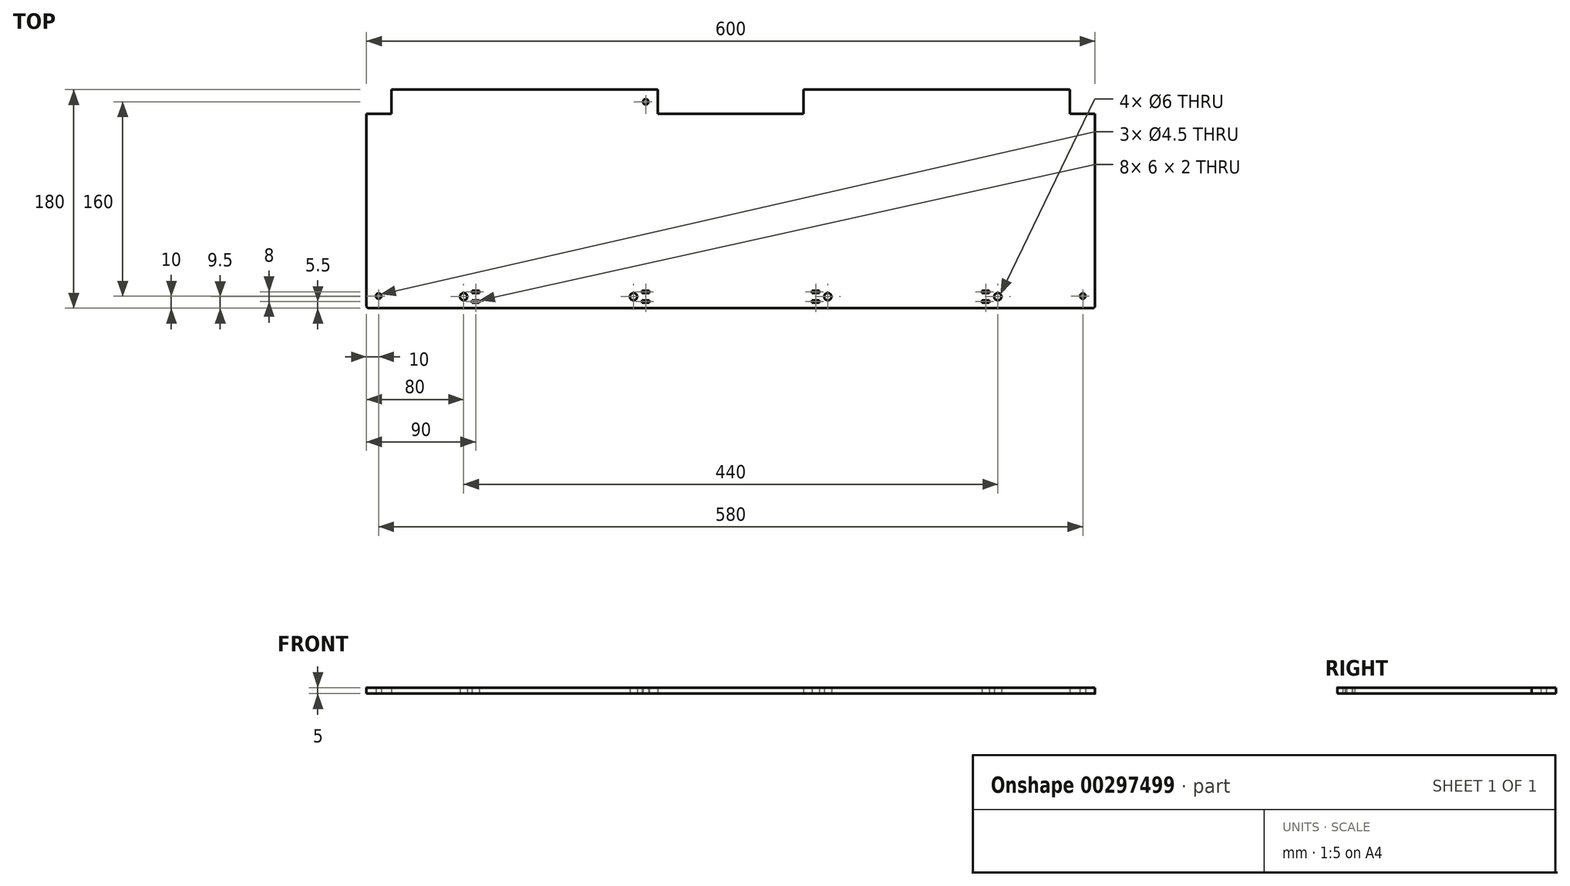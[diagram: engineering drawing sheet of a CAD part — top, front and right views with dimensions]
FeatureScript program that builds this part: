
annotation { "Feature Type Name" : "Feature", "Feature Type Description" : "" }
export const myFeature = defineFeature(function(context is Context, id is Id, definition is map)
    precondition{}
    {
        {
            var Q0;
            Q0=qCreatedBy(makeId("Top.planeOp"),FACE);
            var sketch = newSketch(context, id + "F0", { "sketchPlane" : qUnion([Q0])});
            skCircle(sketch, "E0", {"center": v(-70, 0) * mm, "radius": 3 * mm});
            skCircle(sketch, "E1.MirrorC", {"center": v(70, 0) * mm, "radius": 3 * mm});
            skCircle(sketch, "E2", {"center": v(230, 0) * mm, "radius": 3 * mm});
            skCircle(sketch, "E3.MirrorC", {"center": v(370, 0) * mm, "radius": 3 * mm});
            skLineSegment(sketch, "E4.bottom", {"start": v(-148, -9.5) * mm, "end": v(448, -9.5) * mm});
            skLineSegment(sketch, "E4.left", {"start": v(-150, -7.5) * mm, "end": v(-150, 150.5) * mm});
            skLineSegment(sketch, "E4.right", {"start": v(450, -7.5) * mm, "end": v(450, 150.5) * mm});
            skPoint(sketch, "E5.visualSharp", {"position": v(-150, -9.5) * mm});
            skArc(sketch, "E5.filletArc", {"start": v(-150, -7.5) * mm, "mid": v(-149.41, -8.91) * mm, "end": v(-148, -9.5) * mm});
            skPoint(sketch, "E6.visualSharp", {"position": v(450, -9.5) * mm});
            skArc(sketch, "E6.filletArc", {"start": v(448, -9.5) * mm, "mid": v(449.41, -8.91) * mm, "end": v(450, -7.5) * mm});
            skLineSegment(sketch, "E7", {"start": v(-129.5, 170.5) * mm, "end": v(90, 170.5) * mm});
            skLineSegment(sketch, "E8.top", {"start": v(-150, 150.5) * mm, "end": v(-129.5, 150.5) * mm});
            skLineSegment(sketch, "E8.right", {"start": v(-129.5, 170.5) * mm, "end": v(-129.5, 150.5) * mm});
            skLineSegment(sketch, "E9.top", {"start": v(450, 150.5) * mm, "end": v(429.5, 150.5) * mm});
            skLineSegment(sketch, "E9.right", {"start": v(429.5, 170.5) * mm, "end": v(429.5, 150.5) * mm});
            skLineSegment(sketch, "E10.top", {"start": v(210, 150.5) * mm, "end": v(90, 150.5) * mm});
            skLineSegment(sketch, "E10.left", {"start": v(210, 170.5) * mm, "end": v(210, 150.5) * mm});
            skLineSegment(sketch, "E10.right", {"start": v(90, 170.5) * mm, "end": v(90, 150.5) * mm});
            skPoint(sketch, "E10.middle", {"position": v(150, 160.5) * mm});
            skPoint(sketch, "E10.middle.positionSnap0", {"position": v(150, 170.5) * mm});
            skPoint(sketch, "E10.centerSnap0", {"position": v(150, 170.5) * mm});
            skPoint(sketch, "E11.orphan", {"position": v(-150, 170.5) * mm});
            skLineSegment(sketch, "E12.trimOffspring", {"start": v(210, 170.5) * mm, "end": v(429.5, 170.5) * mm});
            skPoint(sketch, "E13.orphan", {"position": v(450, 170.5) * mm});
            skCircle(sketch, "E14", {"center": v(-140, 0.5) * mm, "radius": 2.25 * mm});
            skCircle(sketch, "E15", {"center": v(440, 0.5) * mm, "radius": 2.25 * mm});
            skCircle(sketch, "E16", {"center": v(80, 160.5) * mm, "radius": 2.25 * mm});
            skLineSegment(sketch, "E17.bottom", {"start": v(-63, 5) * mm, "end": v(-57, 5) * mm});
            skLineSegment(sketch, "E17.top", {"start": v(-63, 3) * mm, "end": v(-57, 3) * mm});
            skLineSegment(sketch, "E17.left", {"start": v(-63, 5) * mm, "end": v(-63, 3) * mm});
            skLineSegment(sketch, "E17.right", {"start": v(-57, 5) * mm, "end": v(-57, 3) * mm});
            skLineSegment(sketch, "E18.bottom", {"start": v(-63, -3) * mm, "end": v(-57, -3) * mm});
            skLineSegment(sketch, "E18.top", {"start": v(-63, -5) * mm, "end": v(-57, -5) * mm});
            skLineSegment(sketch, "E18.left", {"start": v(-63, -3) * mm, "end": v(-63, -5) * mm});
            skLineSegment(sketch, "E18.right", {"start": v(-57, -3) * mm, "end": v(-57, -5) * mm});
            skLineSegment(sketch, "E19.bottom", {"start": v(77, 5) * mm, "end": v(83, 5) * mm});
            skLineSegment(sketch, "E19.top", {"start": v(77, 3) * mm, "end": v(83, 3) * mm});
            skLineSegment(sketch, "E19.left", {"start": v(77, 5) * mm, "end": v(77, 3) * mm});
            skLineSegment(sketch, "E19.right", {"start": v(83, 5) * mm, "end": v(83, 3) * mm});
            skLineSegment(sketch, "E20.bottom", {"start": v(77, -3) * mm, "end": v(83, -3) * mm});
            skLineSegment(sketch, "E20.top", {"start": v(77, -5) * mm, "end": v(83, -5) * mm});
            skLineSegment(sketch, "E20.left", {"start": v(77, -3) * mm, "end": v(77, -5) * mm});
            skLineSegment(sketch, "E20.right", {"start": v(83, -3) * mm, "end": v(83, -5) * mm});
            skPoint(sketch, "E21", {"position": v(-50, 0) * mm});
            skLineSegment(sketch, "E22.bottom", {"start": v(357, 5) * mm, "end": v(363, 5) * mm});
            skLineSegment(sketch, "E22.top", {"start": v(357, 3) * mm, "end": v(363, 3) * mm});
            skLineSegment(sketch, "E22.left", {"start": v(357, 5) * mm, "end": v(357, 3) * mm});
            skLineSegment(sketch, "E22.right", {"start": v(363, 5) * mm, "end": v(363, 3) * mm});
            skLineSegment(sketch, "E23.bottom", {"start": v(357, -3) * mm, "end": v(363, -3) * mm});
            skLineSegment(sketch, "E23.top", {"start": v(357, -5) * mm, "end": v(363, -5) * mm});
            skLineSegment(sketch, "E23.left", {"start": v(357, -3) * mm, "end": v(357, -5) * mm});
            skLineSegment(sketch, "E23.right", {"start": v(363, -3) * mm, "end": v(363, -5) * mm});
            skLineSegment(sketch, "E24.bottom", {"start": v(217, 5) * mm, "end": v(223, 5) * mm});
            skLineSegment(sketch, "E24.top", {"start": v(217, 3) * mm, "end": v(223, 3) * mm});
            skLineSegment(sketch, "E24.left", {"start": v(217, 5) * mm, "end": v(217, 3) * mm});
            skLineSegment(sketch, "E24.right", {"start": v(223, 5) * mm, "end": v(223, 3) * mm});
            skLineSegment(sketch, "E25.bottom", {"start": v(217, -3) * mm, "end": v(223, -3) * mm});
            skLineSegment(sketch, "E25.top", {"start": v(217, -5) * mm, "end": v(223, -5) * mm});
            skLineSegment(sketch, "E25.left", {"start": v(217, -3) * mm, "end": v(217, -5) * mm});
            skLineSegment(sketch, "E25.right", {"start": v(223, -3) * mm, "end": v(223, -5) * mm});
            skPoint(sketch, "E26", {"position": v(150, -9.5) * mm});
            skSolve(sketch);
        }
        {
            var Q0;
            Q0=makeQuery(id+"F0.imprint","IMPRINT",FACE,{"disambiguationData":[TD([[makeQuery(id+"F0.imprint","IMPRINT",EDGE,{"derivedFrom":sQuery(id+"F0.wireOp",EDGE,"E0")}),-1.0]])]});
            extrude(context, id + "F1", {"entities" : qUnion([Q0]), "depth" : 5 * mm});
        }
    });
